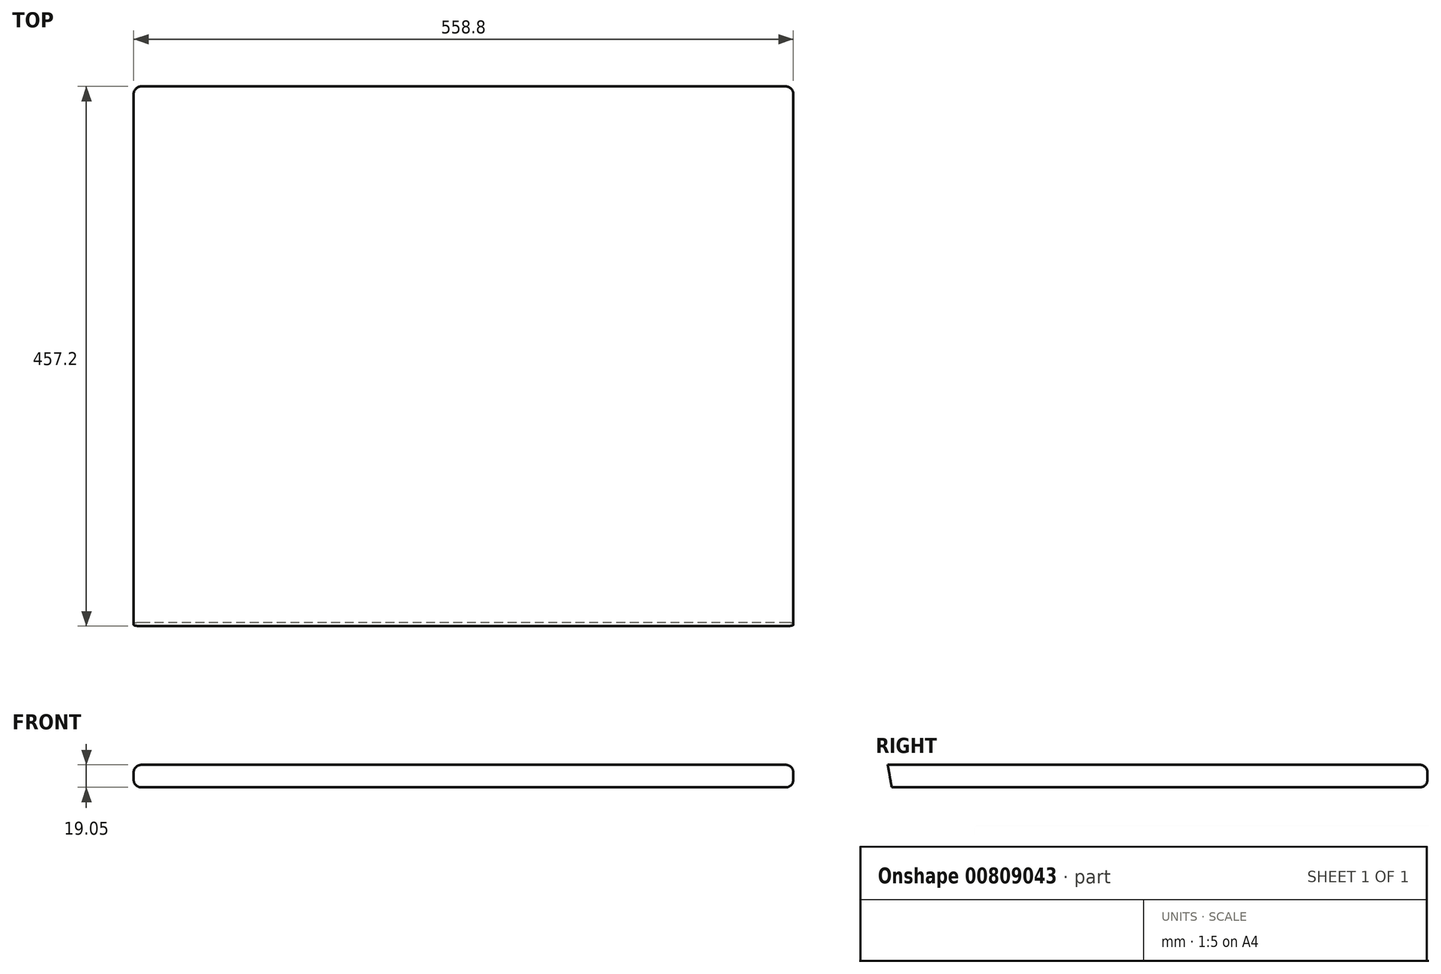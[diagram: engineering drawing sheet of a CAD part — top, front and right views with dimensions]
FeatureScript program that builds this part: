
annotation { "Feature Type Name" : "Feature", "Feature Type Description" : "" }
export const myFeature = defineFeature(function(context is Context, id is Id, definition is map)
    precondition{}
    {
        {
            var Q0;
            Q0=qCreatedBy(makeId("Top.planeOp"),FACE);
            var sketch = newSketch(context, id + "F0", { "sketchPlane" : qUnion([Q0])});
            skLineSegment(sketch, "E0.bottom", {"start": v(0, 0) * mm, "end": v(558.8, 0) * mm});
            skLineSegment(sketch, "E0.top", {"start": v(0, 457.2) * mm, "end": v(558.8, 457.2) * mm});
            skLineSegment(sketch, "E0.left", {"start": v(0, 0) * mm, "end": v(0, 457.2) * mm});
            skLineSegment(sketch, "E0.right", {"start": v(558.8, 0) * mm, "end": v(558.8, 457.2) * mm});
            skSolve(sketch);
        }
        {
            var Q0;
            Q0 = qSketchRegion(id + "F0", true);
            extrude(context, id + "F1", {"entities" : qUnion([Q0]), "flatOperationType" : FlatOperationType.REMOVE, "depth" : 19.05 * mm, "offsetDistance" : 25.4 * mm, "domain" : OperationDomain.MODEL});
        }
        {
            var Q0;
            Q0=makeQuery(id+"F1.opExtrude","SWEPT_FACE",FACE,{"disambiguationData":[OSD([sQuery(id+"F0.wireOp",EDGE,"E0.right")])]});
            var sketch = newSketch(context, id + "F2", { "sketchPlane" : qUnion([Q0])});
            skLineSegment(sketch, "E1", {"start": v(0, 19.05) * mm, "end": v(3.36, 0) * mm});
            skLineSegment(sketch, "E2", {"start": v(3.36, 0) * mm, "end": v(0, 0) * mm});
            skLineSegment(sketch, "E3", {"start": v(0, 0) * mm, "end": v(0, 19.05) * mm});
            skSolve(sketch);
        }
        {
            var Q0;
            Q0 = qSketchRegion(id + "F2", true);
            extrude(context, id + "F3", {"entities" : qUnion([Q0]), "operationType" : NewBodyOperationType.REMOVE, "endBound" : BoundingType.THROUGH_ALL, "oppositeDirection" : true, "depth" : 25.4 * mm, "offsetDistance" : 25.4 * mm});
        }
        {
            var Q0;
            Q0=makeQuery(id+"F1.opExtrude","CAP_EDGE",EDGE,{"disambiguationData":[OSD([sQuery(id+"F0.wireOp",EDGE,"E0.right")])],"isStart":false});
            var Q1;
            Q1=makeQuery(id+"F1.opExtrude","CAP_EDGE",EDGE,{"disambiguationData":[OSD([sQuery(id+"F0.wireOp",EDGE,"E0.right")])],"isStart":true});
            var Q2;
            Q2=makeQuery(id+"F1.opExtrude","SWEPT_EDGE",EDGE,{"disambiguationData":[OSD([sQuery(id+"F0.wireOp",EDGE,"E0.top"),sQuery(id+"F0.wireOp",EDGE,"E0.right")])]});
            var Q3;
            Q3=makeQuery(id+"F1.opExtrude","CAP_EDGE",EDGE,{"disambiguationData":[OSD([sQuery(id+"F0.wireOp",EDGE,"E0.top")])],"isStart":false});
            var Q4;
            Q4=makeQuery(id+"F1.opExtrude","CAP_EDGE",EDGE,{"disambiguationData":[OSD([sQuery(id+"F0.wireOp",EDGE,"E0.top")])],"isStart":true});
            var Q5;
            Q5=makeQuery(id+"F1.opExtrude","SWEPT_EDGE",EDGE,{"disambiguationData":[OSD([sQuery(id+"F0.wireOp",EDGE,"E0.top"),sQuery(id+"F0.wireOp",EDGE,"E0.left")])]});
            var Q6;
            Q6=makeQuery(id+"F1.opExtrude","CAP_EDGE",EDGE,{"disambiguationData":[OSD([sQuery(id+"F0.wireOp",EDGE,"E0.left")])],"isStart":false});
            var Q7;
            Q7=makeQuery(id+"F1.opExtrude","CAP_EDGE",EDGE,{"disambiguationData":[OSD([sQuery(id+"F0.wireOp",EDGE,"E0.left")])],"isStart":true});
            fillet(context, id + "F4", {"entities" : qUnion([Q0, Q1, Q2, Q3, Q4, Q5, Q6, Q7]), "radius" : 6.35 * mm, "tangentPropagation" : true, "allowEdgeOverflow" : false});
        }
    });
